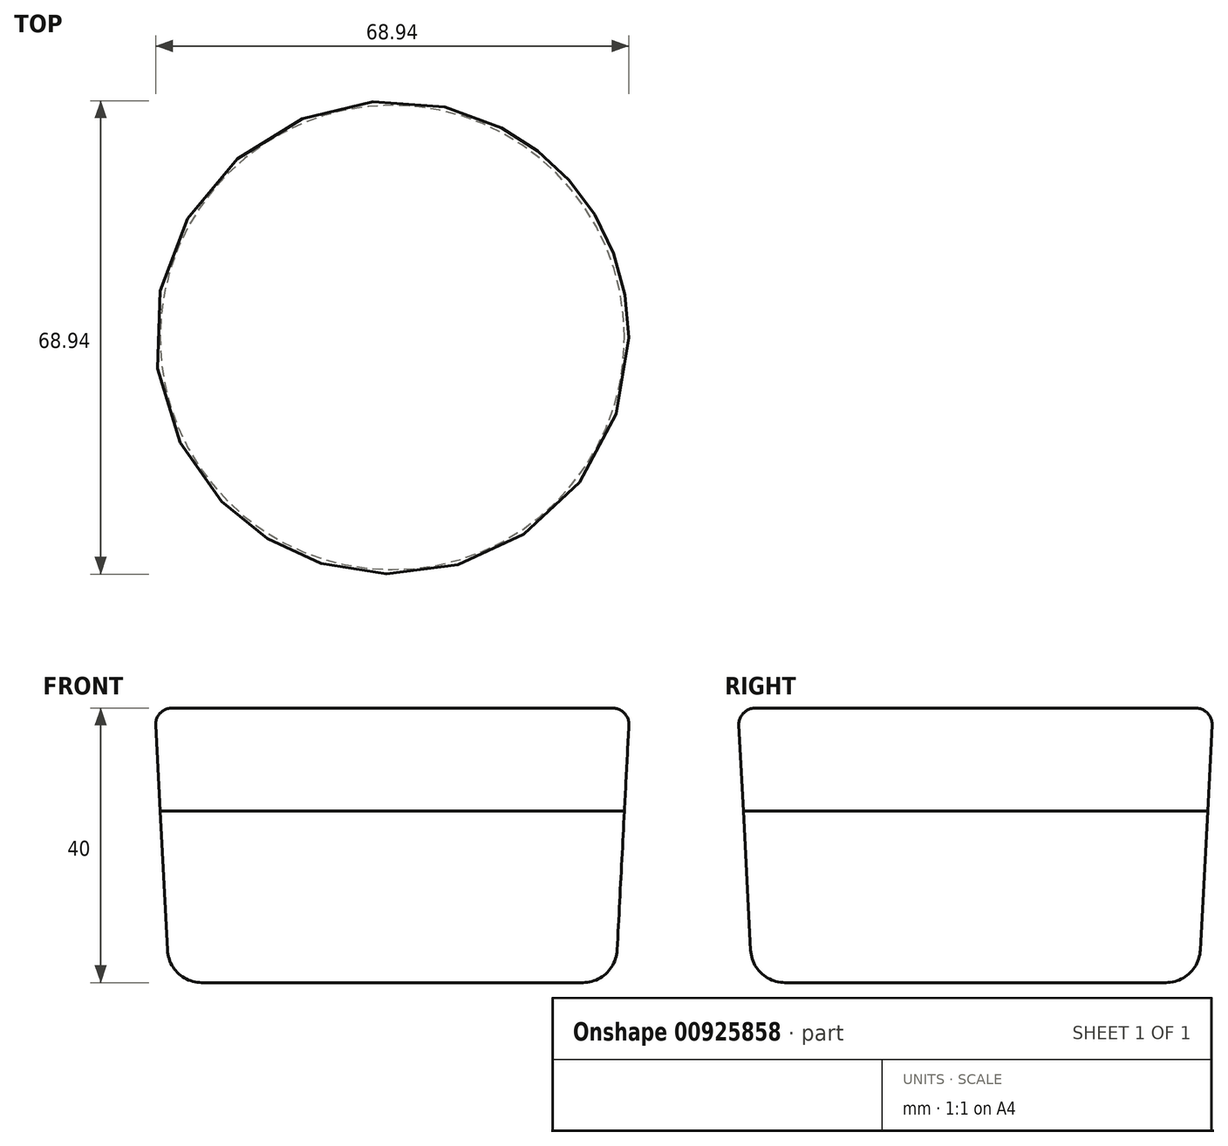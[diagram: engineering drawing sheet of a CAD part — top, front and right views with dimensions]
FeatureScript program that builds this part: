
annotation { "Feature Type Name" : "Feature", "Feature Type Description" : "" }
export const myFeature = defineFeature(function(context is Context, id is Id, definition is map)
    precondition{}
    {
        {
            var Q0;
            Q0=qCreatedBy(makeId("Top.planeOp"),FACE);
            var sketch = newSketch(context, id + "F0", { "sketchPlane" : qUnion([Q0])});
            skCircle(sketch, "E0", {"center": v(0, 0) * mm, "radius": 32.5 * mm});
            skSolve(sketch);
        }
        {
            var Q0;
            Q0 = qSketchRegion(id + "F0", true);
            extrude(context, id + "F1", {"entities" : qUnion([Q0]), "depth" : 25 * mm, "offsetDistance" : 25 * mm, "hasDraft" : true, "draftAngle" : 3 * degree});
        }
        {
            var Q0;
            Q0=makeQuery(id+"F1.opExtrude","CAP_FACE",FACE,{"disambiguationData":[OSD([sQuery(id+"F0.wireOp",EDGE,"E0")])],"isStart":false});
            var sketch = newSketch(context, id + "F2", { "sketchPlane" : qUnion([Q0])});
            skCircle(sketch, "E1.0", {"center": v(0, 0) * mm, "radius": 33.81 * mm});
            skSolve(sketch);
        }
        {
            var Q0;
            Q0 = qSketchRegion(id + "F2", true);
            extrude(context, id + "F3", {"entities" : qUnion([Q0]), "depth" : 15 * mm, "offsetDistance" : 25 * mm, "hasDraft" : true, "draftAngle" : 3 * degree});
        }
        {
            var Q0;
            Q0=makeQuery(id+"F3.opExtrude","CAP_EDGE",EDGE,{"disambiguationData":[OSD([sQuery(id+"F2.wireOp",EDGE,"E1.0")])],"isStart":false});
            fillet(context, id + "F4", {"entities" : qUnion([Q0]), "radius" : 2.4 * mm, "tangentPropagation" : true, "allowEdgeOverflow" : false});
        }
        {
            var Q0;
            Q0=makeQuery(id+"F1.opExtrude","CAP_EDGE",EDGE,{"disambiguationData":[OSD([sQuery(id+"F0.wireOp",EDGE,"E0")])],"isStart":true});
            fillet(context, id + "F5", {"entities" : qUnion([Q0]), "radius" : 5 * mm, "tangentPropagation" : true, "allowEdgeOverflow" : false});
        }
    });
